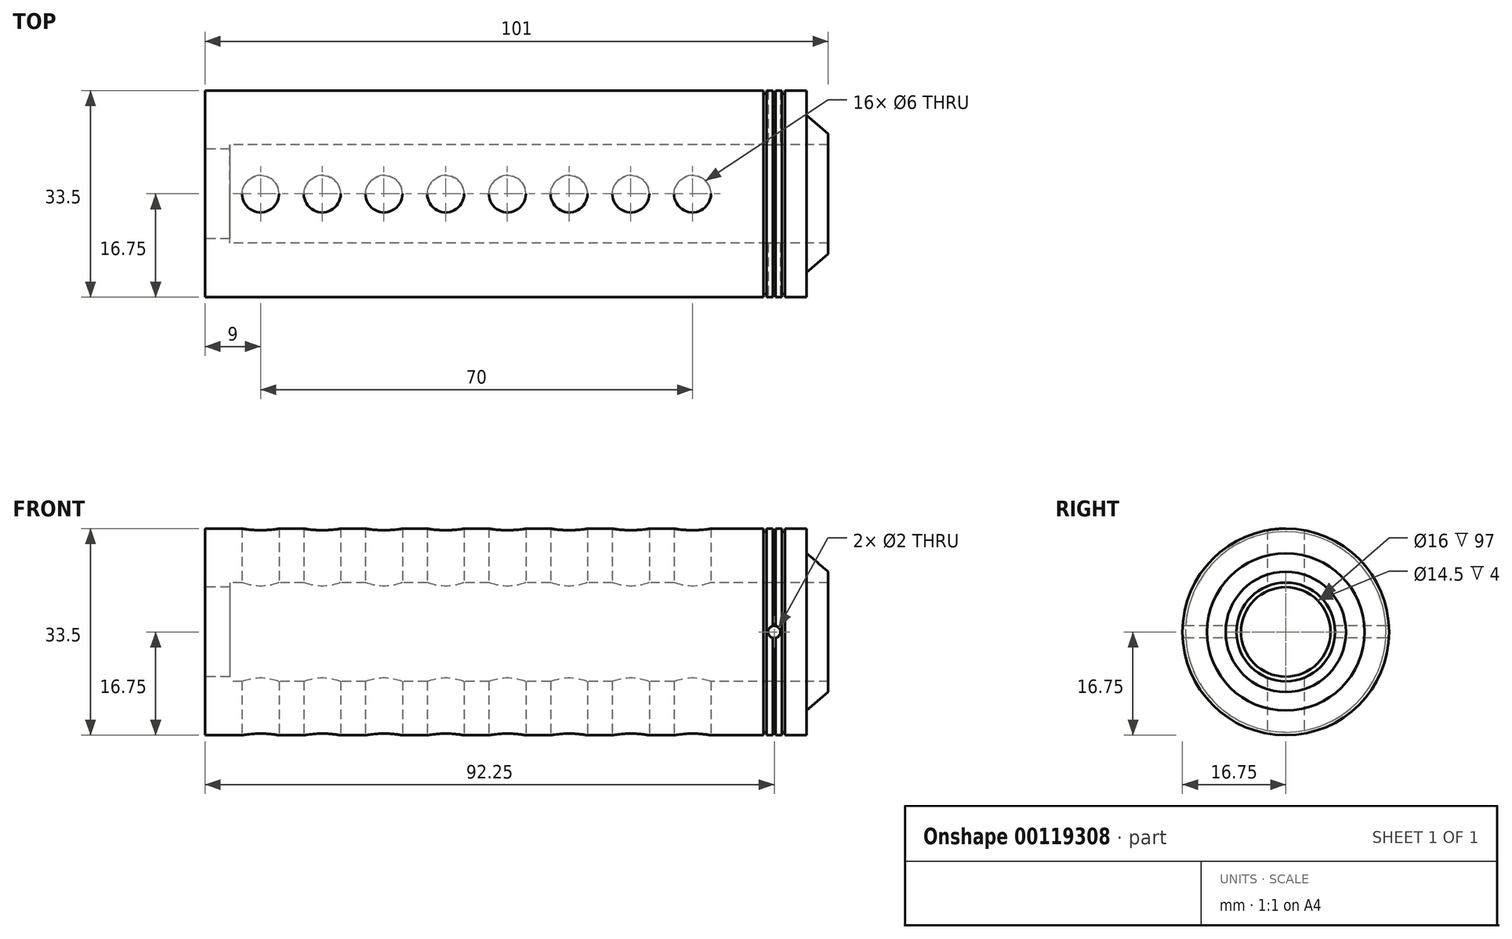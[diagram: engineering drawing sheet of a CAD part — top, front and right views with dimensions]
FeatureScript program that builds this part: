
annotation { "Feature Type Name" : "Feature", "Feature Type Description" : "" }
export const myFeature = defineFeature(function(context is Context, id is Id, definition is map)
    precondition{}
    {
        {
            var Q0;
            Q0=qCreatedBy(makeId("Front.planeOp"),FACE);
            var sketch = newSketch(context, id + "F0", { "sketchPlane" : qUnion([Q0])});
            skLineSegment(sketch, "E0", {"start": v(0, 0) * mm, "end": v(0, -16.75) * mm});
            skLineSegment(sketch, "E1", {"start": v(0, -16.75) * mm, "end": v(90.5, -16.75) * mm});
            skLineSegment(sketch, "E2", {"start": v(97.5, -16.75) * mm, "end": v(97.5, -12.75) * mm});
            skLineSegment(sketch, "E3", {"start": v(101, -8) * mm, "end": v(101, -9.75) * mm});
            skLineSegment(sketch, "E4", {"start": v(101, -9.75) * mm, "end": v(97.5, -12.75) * mm});
            skLineSegment(sketch, "E5", {"start": v(94, 3.53) * mm, "end": v(94, 0) * mm, "construction": true});
            skLineSegment(sketch, "E6", {"start": v(93.5, 3.88) * mm, "end": v(93.5, 0) * mm, "construction": true});
            skLineSegment(sketch, "E7.0", {"start": v(90.5, -16.25) * mm, "end": v(91, -16.25) * mm});
            skLineSegment(sketch, "E8.0", {"start": v(92.5, 3.88) * mm, "end": v(92.5, 0) * mm});
            skLineSegment(sketch, "E9.0", {"start": v(92, 3.88) * mm, "end": v(92, 0) * mm});
            skLineSegment(sketch, "E10.0", {"start": v(91, 3.88) * mm, "end": v(91, 0) * mm});
            skLineSegment(sketch, "E11.0", {"start": v(90.5, 3.88) * mm, "end": v(90.5, 0) * mm});
            skLineSegment(sketch, "E12", {"start": v(94, -16.75) * mm, "end": v(94, -16.25) * mm});
            skLineSegment(sketch, "E13", {"start": v(93.5, -16.75) * mm, "end": v(93.5, -16.25) * mm});
            skLineSegment(sketch, "E14.trimOffspring", {"start": v(92.5, -16.75) * mm, "end": v(93.5, -16.75) * mm});
            skLineSegment(sketch, "E15.trimOffspring", {"start": v(90.5, -16.25) * mm, "end": v(90.5, -16.75) * mm});
            skLineSegment(sketch, "E16.trimOffspring", {"start": v(91, -16.25) * mm, "end": v(91, -16.75) * mm});
            skLineSegment(sketch, "E17.trimOffspring", {"start": v(92, -16.25) * mm, "end": v(92, -16.75) * mm});
            skLineSegment(sketch, "E18.trimOffspring", {"start": v(92.5, -16.25) * mm, "end": v(92.5, -16.75) * mm});
            skLineSegment(sketch, "E19.trimOffspring", {"start": v(93.5, -16.25) * mm, "end": v(93.5, -21.89) * mm, "construction": true});
            skLineSegment(sketch, "E20.trimOffspring", {"start": v(94, -16.25) * mm, "end": v(94, -21.24) * mm, "construction": true});
            skLineSegment(sketch, "E21.trimOffspring", {"start": v(94, -16.75) * mm, "end": v(97.5, -16.75) * mm});
            skLineSegment(sketch, "E22.trimOffspring", {"start": v(93.5, -16.25) * mm, "end": v(94, -16.25) * mm});
            skLineSegment(sketch, "E23.trimOffspring", {"start": v(92, -16.25) * mm, "end": v(92.5, -16.25) * mm});
            skLineSegment(sketch, "E24.trimOffspring", {"start": v(91, -16.75) * mm, "end": v(92, -16.75) * mm});
            skLineSegment(sketch, "E25.0", {"start": v(101, -8) * mm, "end": v(4, -8) * mm});
            skLineSegment(sketch, "E26", {"start": v(0, 0) * mm, "end": v(4, 0) * mm});
            skLineSegment(sketch, "E27", {"start": v(4, 0) * mm, "end": v(4, -8) * mm});
            skSolve(sketch);
        }
        {
            var Q0;
            Q0 = qSketchRegion(id + "F0", true);
            var Q1;
            Q1=sQuery(id+"F0.wireOp",EDGE,"E26");
            revolve(context, id + "F1", {"entities" : qUnion([Q0]), "axis" : qUnion([Q1]), "revolveType" : RevolveType.FULL});
        }
        {
            var Q0;
            Q0=qCreatedBy(makeId("Front.planeOp"),FACE);
            var sketch = newSketch(context, id + "F2", { "sketchPlane" : qUnion([Q0])});
            skLineSegment(sketch, "E28", {"start": v(69.11, 0) * mm, "end": v(107.74, 0) * mm, "construction": true});
            skCircle(sketch, "E29", {"center": v(92.25, 0) * mm, "radius": 1 * mm});
            skSolve(sketch);
        }
        {
            var Q0;
            Q0 = qSketchRegion(id + "F2", true);
            extrude(context, id + "F3", {"entities" : qUnion([Q0]), "operationType" : NewBodyOperationType.REMOVE, "endBound" : BoundingType.SYMMETRIC, "oppositeDirection" : true, "depth" : 50 * mm});
        }
        {
            var Q0;
            Q0=makeQuery(id+"F1.opRevolve","SWEPT_FACE",FACE,{"disambiguationData":[OSD([sQuery(id+"F0.wireOp",EDGE,"E0")])]});
            var sketch = newSketch(context, id + "F4", { "sketchPlane" : qUnion([Q0])});
            skCircle(sketch, "E30", {"center": v(0, 0) * mm, "radius": 7.25 * mm});
            skSolve(sketch);
        }
        {
            var Q0;
            Q0 = qSketchRegion(id + "F4", true);
            extrude(context, id + "F5", {"entities" : qUnion([Q0]), "operationType" : NewBodyOperationType.REMOVE, "oppositeDirection" : true, "depth" : 2.5 * mm});
        }
        {
            var Q0;
            Q0=qCreatedBy(makeId("Top.planeOp"),FACE);
            var sketch = newSketch(context, id + "F6", { "sketchPlane" : qUnion([Q0])});
            skLineSegment(sketch, "E31", {"start": v(9, 18.99) * mm, "end": v(9, -20.5) * mm, "construction": true});
            skLineSegment(sketch, "E32.0", {"start": v(19, 18.99) * mm, "end": v(19, -20.5) * mm});
            skLineSegment(sketch, "E33.0", {"start": v(29, 18.99) * mm, "end": v(29, -20.5) * mm});
            skLineSegment(sketch, "E34.0", {"start": v(39, 18.99) * mm, "end": v(39, -20.5) * mm});
            skLineSegment(sketch, "E35.0", {"start": v(49, 18.99) * mm, "end": v(49, -20.5) * mm});
            skLineSegment(sketch, "E36.0", {"start": v(59, 18.99) * mm, "end": v(59, -20.5) * mm});
            skLineSegment(sketch, "E37.0", {"start": v(69, 18.99) * mm, "end": v(69, -20.5) * mm});
            skLineSegment(sketch, "E38.0", {"start": v(79, 18.99) * mm, "end": v(79, -20.5) * mm});
            skCircle(sketch, "E39", {"center": v(9, 0) * mm, "radius": 3 * mm});
            skCircle(sketch, "E40", {"center": v(19, 0) * mm, "radius": 3 * mm});
            skCircle(sketch, "E41", {"center": v(29, 0) * mm, "radius": 3 * mm});
            skCircle(sketch, "E42", {"center": v(39, 0) * mm, "radius": 3 * mm});
            skCircle(sketch, "E43", {"center": v(49, 0) * mm, "radius": 3 * mm});
            skCircle(sketch, "E44", {"center": v(59, 0) * mm, "radius": 3 * mm});
            skCircle(sketch, "E45", {"center": v(69, 0) * mm, "radius": 3 * mm});
            skCircle(sketch, "E46", {"center": v(79, 0) * mm, "radius": 3 * mm});
            skSolve(sketch);
        }
        {
            var Q0;
            Q0 = qSketchRegion(id + "F6", true);
            extrude(context, id + "F7", {"entities" : qUnion([Q0]), "operationType" : NewBodyOperationType.REMOVE, "endBound" : BoundingType.SYMMETRIC, "depth" : 50 * mm});
        }
        {
            var Q0;
            Q0=makeQuery(id+"F5.boolean.opBoolean","COPY",FACE,{"derivedFrom":makeQuery(id+"F5.opExtrude","CAP_FACE",FACE,{"disambiguationData":[OSD([sQuery(id+"F4.wireOp",EDGE,"E30")])],"isStart":false})});
            var sketch = newSketch(context, id + "F8", { "sketchPlane" : qUnion([Q0])});
            skCircle(sketch, "E47.0", {"center": v(0, 0) * mm, "radius": 7.25 * mm});
            skSolve(sketch);
        }
        {
            var Q0;
            Q0 = qSketchRegion(id + "F8", true);
            extrude(context, id + "F9", {"entities" : qUnion([Q0]), "operationType" : NewBodyOperationType.REMOVE, "oppositeDirection" : true, "depth" : 25 * mm});
        }
    });
